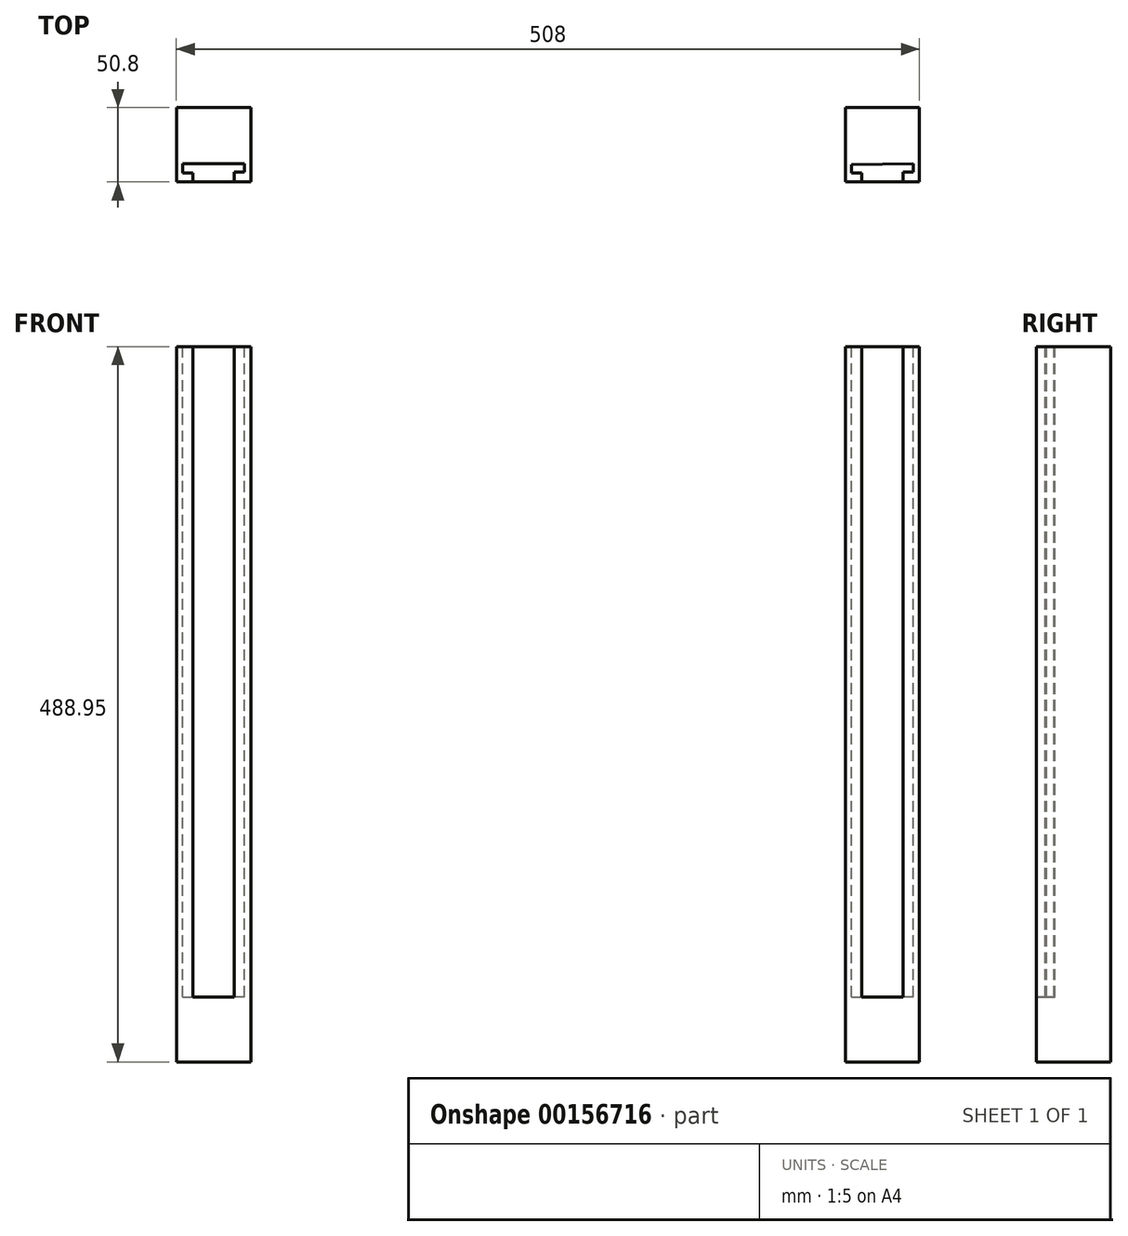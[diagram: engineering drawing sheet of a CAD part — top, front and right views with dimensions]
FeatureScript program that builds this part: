
annotation { "Feature Type Name" : "Feature", "Feature Type Description" : "" }
export const myFeature = defineFeature(function(context is Context, id is Id, definition is map)
    precondition{}
    {
        {
            var Q0;
            Q0=qCreatedBy(makeId("Front.planeOp"),FACE);
            var sketch = newSketch(context, id + "F0", { "sketchPlane" : qUnion([Q0])});
            skLineSegment(sketch, "E0.bottom", {"start": v(-241.12, 387.24) * mm, "end": v(266.88, 387.24) * mm});
            skLineSegment(sketch, "E0.top", {"start": v(-241.12, 368.2) * mm, "end": v(266.88, 368.2) * mm});
            skLineSegment(sketch, "E0.left", {"start": v(-241.12, 387.24) * mm, "end": v(-241.12, 368.2) * mm});
            skLineSegment(sketch, "E0.right", {"start": v(266.88, 387.24) * mm, "end": v(266.88, 368.2) * mm});
            skLineSegment(sketch, "E1", {"start": v(-241.12, 368.2) * mm, "end": v(-241.12, -120.76) * mm});
            skLineSegment(sketch, "E2", {"start": v(266.88, 368.2) * mm, "end": v(266.88, -120.76) * mm});
            skLineSegment(sketch, "E3", {"start": v(-241.12, -120.76) * mm, "end": v(-190.32, -120.76) * mm});
            skLineSegment(sketch, "E4", {"start": v(-190.32, -120.76) * mm, "end": v(-190.32, 368.2) * mm});
            skLineSegment(sketch, "E5", {"start": v(266.88, -120.76) * mm, "end": v(216.08, -120.76) * mm});
            skLineSegment(sketch, "E6", {"start": v(216.08, -120.76) * mm, "end": v(216.08, 368.2) * mm});
            skSolve(sketch);
        }
        {
            var Q0;
            {var subQ0=sQuery(id+"F0.wireOp",EDGE,"E1");Q0=makeQuery(id+"F0.imprint","IMPRINT",FACE,{"disambiguationData":[TD([[makeQuery(id+"F0.imprint","IMPRINT",EDGE,{"derivedFrom":subQ0}),1.0]])]});}
            var Q1;
            {var subQ0=sQuery(id+"F0.wireOp",EDGE,"E2");Q1=makeQuery(id+"F0.imprint","IMPRINT",FACE,{"disambiguationData":[TD([[makeQuery(id+"F0.imprint","IMPRINT",EDGE,{"derivedFrom":subQ0}),-1.0]])]});}
            extrude(context, id + "F1", {"entities" : qUnion([Q0, Q1]), "depth" : 50.8 * mm});
        }
        {
            var Q0;
            {var subQ0=sQuery(id+"F0.wireOp",EDGE,"E0.top");Q0=makeQuery(id+"F1.opExtrude","SWEPT_FACE",FACE,{"disambiguationData":[OSD([subQ0]),TDD([makeQuery(id+"F0.imprint","IMPRINT",EDGE,{"disambiguationData":[TD([[makeQuery(id+"F0.imprint","INTERSECT",VERTEX,{"derivedFrom":[subQ0,sQuery(id+"F0.wireOp",EDGE,"E6")]}),-1.0]])],"derivedFrom":subQ0})])]});}
            var sketch = newSketch(context, id + "F2", { "sketchPlane" : qUnion([Q0])});
            skLineSegment(sketch, "E7", {"start": v(-229.94, -50.8) * mm, "end": v(-229.94, -44.79) * mm});
            skLineSegment(sketch, "E8", {"start": v(-236.8, -44.79) * mm, "end": v(-236.8, -38.35) * mm});
            skPoint(sketch, "E8.startSnap0", {"position": v(-229.94, -44.79) * mm});
            skLineSegment(sketch, "E9", {"start": v(-236.8, -38.35) * mm, "end": v(-194.63, -38.35) * mm});
            skLineSegment(sketch, "E10", {"start": v(-194.63, -38.35) * mm, "end": v(-194.63, -44.12) * mm});
            skLineSegment(sketch, "E11", {"start": v(-194.63, -44.12) * mm, "end": v(-201.5, -44.12) * mm});
            skLineSegment(sketch, "E12", {"start": v(-201.5, -44.12) * mm, "end": v(-201.5, -50.8) * mm});
            skLineSegment(sketch, "E13", {"start": v(-236.8, -44.79) * mm, "end": v(-229.94, -44.79) * mm});
            skLineSegment(sketch, "E14", {"start": v(-229.94, -50.8) * mm, "end": v(-201.5, -50.8) * mm});
            skLineSegment(sketch, "E15", {"start": v(227.26, -50.8) * mm, "end": v(227.26, -44.79) * mm});
            skPoint(sketch, "E16.startSnap0", {"position": v(227.26, -44.79) * mm});
            skLineSegment(sketch, "E17", {"start": v(262.57, -44.12) * mm, "end": v(255.7, -44.12) * mm});
            skLineSegment(sketch, "E18", {"start": v(255.7, -44.12) * mm, "end": v(255.7, -50.8) * mm});
            skLineSegment(sketch, "E19", {"start": v(220.4, -44.79) * mm, "end": v(227.26, -44.79) * mm});
            skLineSegment(sketch, "E20", {"start": v(227.26, -50.8) * mm, "end": v(255.7, -50.8) * mm});
            skLineSegment(sketch, "E21", {"start": v(262.57, -44.12) * mm, "end": v(262.57, -38.35) * mm});
            skLineSegment(sketch, "E22", {"start": v(220.4, -44.79) * mm, "end": v(220.4, -39.02) * mm});
            skLineSegment(sketch, "E23", {"start": v(220.4, -39.02) * mm, "end": v(262.57, -38.35) * mm});
            skSolve(sketch);
        }
        {
            var Q0;
            Q0=makeQuery(id+"F2.imprint","IMPRINT",FACE,{"disambiguationData":[TD([[makeQuery(id+"F2.imprint","IMPRINT",EDGE,{"derivedFrom":sQuery(id+"F2.wireOp",EDGE,"E7")}),-1.0]])]});
            extrude(context, id + "F3", {"entities" : qUnion([Q0]), "operationType" : NewBodyOperationType.REMOVE, "oppositeDirection" : true, "depth" : 444.5 * mm});
        }
        {
            var Q0;
            Q0=makeQuery(id+"F2.imprint","IMPRINT",FACE,{"disambiguationData":[TD([[makeQuery(id+"F2.imprint","IMPRINT",EDGE,{"derivedFrom":sQuery(id+"F2.wireOp",EDGE,"E15")}),-1.0]])]});
            extrude(context, id + "F4", {"entities" : qUnion([Q0]), "operationType" : NewBodyOperationType.REMOVE, "oppositeDirection" : true, "depth" : 444.5 * mm});
        }
    });
